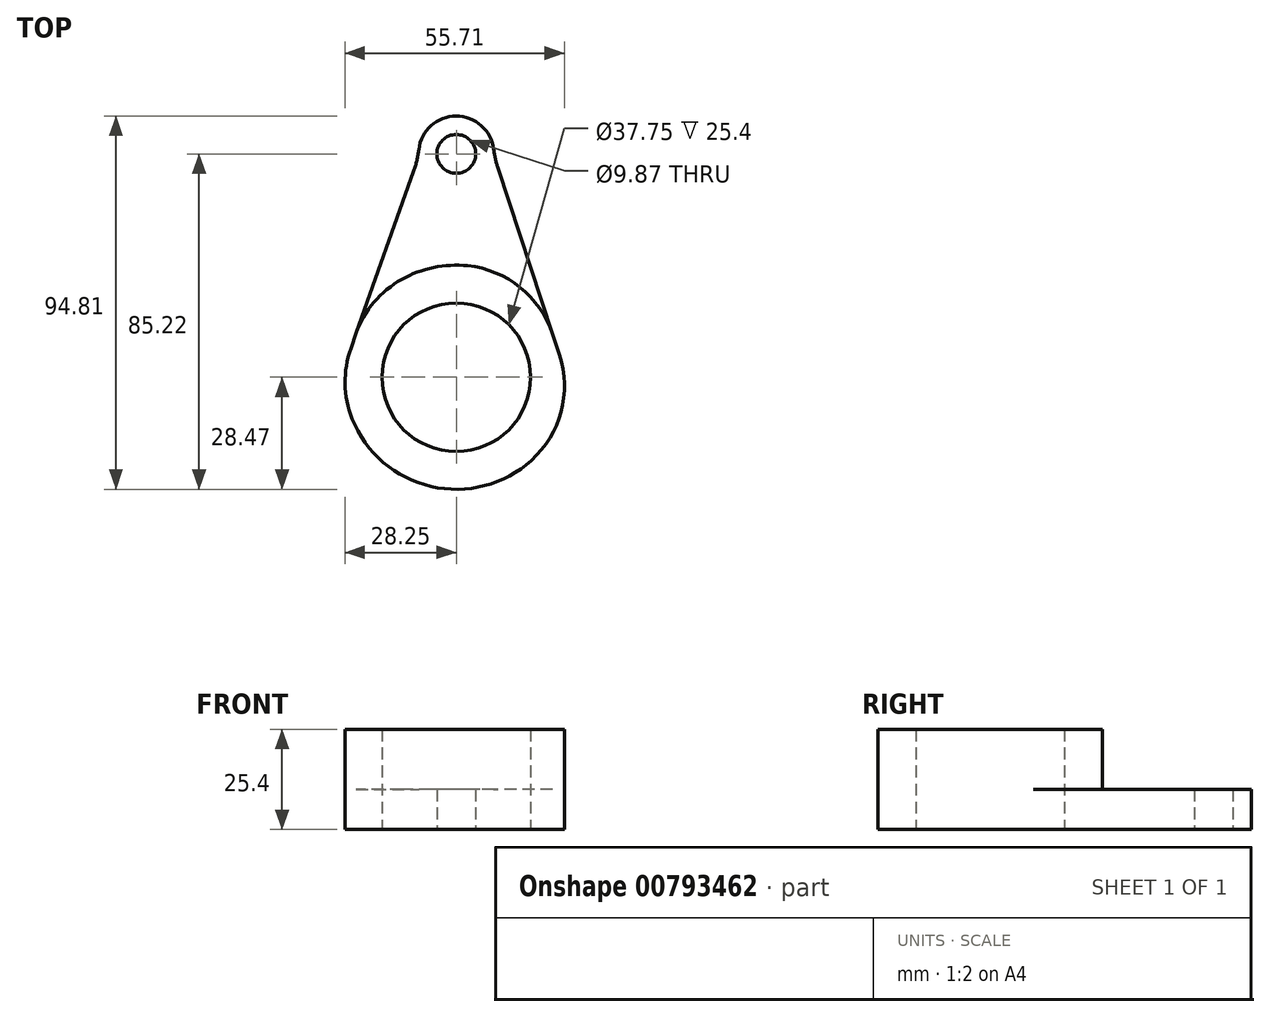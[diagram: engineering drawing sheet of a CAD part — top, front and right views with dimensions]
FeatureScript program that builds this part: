
annotation { "Feature Type Name" : "Feature", "Feature Type Description" : "" }
export const myFeature = defineFeature(function(context is Context, id is Id, definition is map)
    precondition{}
    {
        {
            var Q0;
            Q0=qCreatedBy(makeId("Top.planeOp"),FACE);
            var sketch = newSketch(context, id + "F0", { "sketchPlane" : qUnion([Q0])});
            skArc(sketch, "E0", {"start": v(-28.3, 3.1) * mm, "mid": v(-2.15, -28.39) * mm, "end": v(28.45, -1.21) * mm});
            skCircle(sketch, "E1", {"center": v(0, 0) * mm, "radius": 18.88 * mm});
            skCircle(sketch, "E2", {"center": v(0, 56.75) * mm, "radius": 9.6 * mm});
            skCircle(sketch, "E3", {"center": v(0, 56.75) * mm, "radius": 4.94 * mm});
            skLineSegment(sketch, "E4", {"start": v(-28.3, 3.1) * mm, "end": v(-9.56, 55.92) * mm});
            skLineSegment(sketch, "E5", {"start": v(28.45, -1.21) * mm, "end": v(9.58, 56.25) * mm});
            skArc(sketch, "E6.trimOffspring", {"start": v(22.19, 17.84) * mm, "mid": v(-1.48, 28.43) * mm, "end": v(-23.92, 15.44) * mm});
            skLineSegment(sketch, "E7.trimOffspring", {"start": v(0, 28.47) * mm, "end": v(0, 56.75) * mm});
            skSolve(sketch);
        }
        {
            var Q0;
            {var subQ1=sQuery(id+"F0.wireOp",EDGE,"E0");Q0=makeQuery(id+"F0.imprint","IMPRINT",FACE,{"disambiguationData":[TD([[makeQuery(id+"F0.imprint","IMPRINT",EDGE,{"derivedFrom":subQ1}),1.0]])]});}
            extrude(context, id + "F1", {"entities" : qUnion([Q0]), "depth" : 25.4 * mm, "offsetDistance" : 25.4 * mm});
        }
        {
            var Q0;
            Q0 = qSketchRegion(id + "F0", true);
            extrude(context, id + "F2", {"entities" : qUnion([Q0]), "operationType" : NewBodyOperationType.ADD, "depth" : 10.16 * mm, "offsetDistance" : 25.4 * mm});
        }
        {
            var Q0;
            Q0=makeQuery(id+"F1.opExtrude","SWEPT_EDGE",EDGE,{"disambiguationData":[OSD([sQuery(id+"F0.wireOp",EDGE,"E5"),sQuery(id+"F0.wireOp",EDGE,"E6.trimOffspring")])]});
            var Q1;
            Q1=makeQuery(id+"F1.opExtrude","SWEPT_EDGE",EDGE,{"disambiguationData":[OSD([sQuery(id+"F0.wireOp",EDGE,"E0"),sQuery(id+"F0.wireOp",EDGE,"E5")])]});
            var Q2;
            Q2=makeQuery(id+"F2.opExtrude","SWEPT_EDGE",EDGE,{"disambiguationData":[OSD([sQuery(id+"F0.wireOp",EDGE,"E2"),sQuery(id+"F0.wireOp",EDGE,"E5")])]});
            var Q3;
            Q3=makeQuery(id+"F2.opExtrude","SWEPT_EDGE",EDGE,{"disambiguationData":[OSD([sQuery(id+"F0.wireOp",EDGE,"E2"),sQuery(id+"F0.wireOp",EDGE,"E4")])]});
            var Q4;
            Q4=makeQuery(id+"F1.opExtrude","SWEPT_EDGE",EDGE,{"disambiguationData":[OSD([sQuery(id+"F0.wireOp",EDGE,"E0"),sQuery(id+"F0.wireOp",EDGE,"E4")])]});
            var Q5;
            Q5=makeQuery(id+"F1.opExtrude","SWEPT_EDGE",EDGE,{"disambiguationData":[OSD([sQuery(id+"F0.wireOp",EDGE,"E4"),sQuery(id+"F0.wireOp",EDGE,"E6.trimOffspring")])]});
            fillet(context, id + "F3", {"entities" : qUnion([Q0, Q1, Q2, Q3, Q4, Q5]), "radius" : 25.4 * mm, "tangentPropagation" : true, "allowEdgeOverflow" : false});
        }
    });
